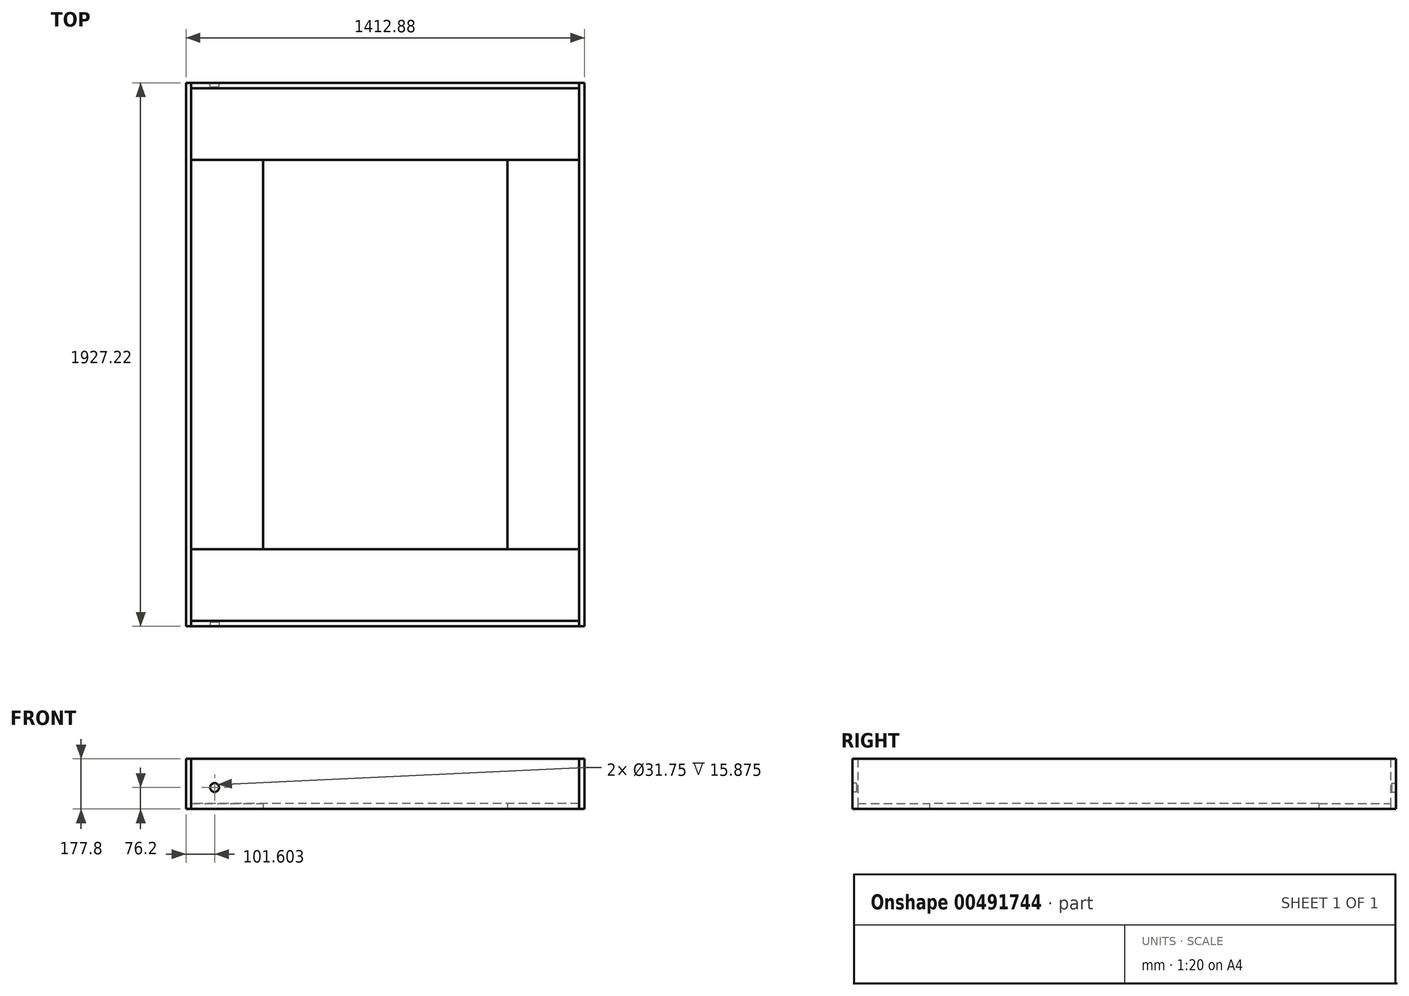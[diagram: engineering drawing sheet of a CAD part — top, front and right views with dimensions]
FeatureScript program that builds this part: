
annotation { "Feature Type Name" : "Feature", "Feature Type Description" : "" }
export const myFeature = defineFeature(function(context is Context, id is Id, definition is map)
    precondition{}
    {
        {
            var Q0;
            Q0=qCreatedBy(makeId("Top.planeOp"),FACE);
            var sketch = newSketch(context, id + "F0", { "sketchPlane" : qUnion([Q0])});
            skLineSegment(sketch, "E0.bottom", {"start": v(687.39, -944.56) * mm, "end": v(-687.39, -944.56) * mm});
            skLineSegment(sketch, "E0.top", {"start": v(687.39, 944.56) * mm, "end": v(-687.39, 944.56) * mm});
            skLineSegment(sketch, "E0.left", {"start": v(687.39, -944.56) * mm, "end": v(687.39, -690.56) * mm});
            skLineSegment(sketch, "E0.right", {"start": v(-687.39, -944.56) * mm, "end": v(-687.39, -690.56) * mm});
            skPoint(sketch, "E0.middle", {"position": v(0, 0) * mm});
            skLineSegment(sketch, "E1", {"start": v(-687.39, -690.56) * mm, "end": v(687.39, -690.56) * mm});
            skLineSegment(sketch, "E2", {"start": v(-687.39, 690.56) * mm, "end": v(687.39, 690.56) * mm});
            skLineSegment(sketch, "E3.trimOffspring", {"start": v(-687.39, 690.56) * mm, "end": v(-687.39, 944.56) * mm});
            skLineSegment(sketch, "E4.trimOffspring", {"start": v(687.39, 690.56) * mm, "end": v(687.39, 944.56) * mm});
            skSolve(sketch);
        }
        {
            var Q0;
            Q0 = qSketchRegion(id + "F0", true);
            extrude(context, id + "F1", {"entities" : qUnion([Q0]), "depth" : 19.05 * mm});
        }
        {
            var Q0;
            Q0=qCreatedBy(makeId("Top.planeOp"),FACE);
            var sketch = newSketch(context, id + "F2", { "sketchPlane" : qUnion([Q0])});
            skLineSegment(sketch, "E5.bottom", {"start": v(-687.39, 690.56) * mm, "end": v(-433.39, 690.56) * mm});
            skLineSegment(sketch, "E5.top", {"start": v(-687.39, -690.56) * mm, "end": v(-433.39, -690.56) * mm});
            skLineSegment(sketch, "E5.left", {"start": v(-687.39, 690.56) * mm, "end": v(-687.39, -690.56) * mm});
            skLineSegment(sketch, "E5.right", {"start": v(-433.39, 690.56) * mm, "end": v(-433.39, -690.56) * mm});
            skLineSegment(sketch, "E6.bottom", {"start": v(687.39, 690.56) * mm, "end": v(433.39, 690.56) * mm});
            skLineSegment(sketch, "E6.top", {"start": v(687.39, -690.56) * mm, "end": v(433.39, -690.56) * mm});
            skLineSegment(sketch, "E6.left", {"start": v(687.39, 690.56) * mm, "end": v(687.39, -690.56) * mm});
            skLineSegment(sketch, "E6.right", {"start": v(433.39, 690.56) * mm, "end": v(433.39, -690.56) * mm});
            skSolve(sketch);
        }
        {
            var Q0;
            Q0 = qSketchRegion(id + "F2", true);
            var Q1;
            Q1=makeQuery(id+"F1.opExtrude","CAP_FACE",FACE,{"disambiguationData":[OSD([sQuery(id+"F0.wireOp",EDGE,"E0.bottom"),sQuery(id+"F0.wireOp",EDGE,"E0.left"),sQuery(id+"F0.wireOp",EDGE,"E0.right"),sQuery(id+"F0.wireOp",EDGE,"E1")])],"isStart":false});
            extrude(context, id + "F3", {"entities" : qUnion([Q0]), "endBound" : BoundingType.UP_TO_SURFACE, "endBoundEntityFace" : qUnion([Q1]), "depth" : 25.4 * mm});
        }
        {
            var Q0;
            Q0=qCreatedBy(makeId("Top.planeOp"),FACE);
            var sketch = newSketch(context, id + "F4", { "sketchPlane" : qUnion([Q0])});
            skLineSegment(sketch, "E7.bottom", {"start": v(-706.44, 963.61) * mm, "end": v(-687.39, 963.61) * mm});
            skLineSegment(sketch, "E7.top", {"start": v(-706.44, -963.61) * mm, "end": v(-687.39, -963.61) * mm});
            skLineSegment(sketch, "E7.left", {"start": v(-706.44, 963.61) * mm, "end": v(-706.44, -963.61) * mm});
            skLineSegment(sketch, "E7.right", {"start": v(-687.39, 963.61) * mm, "end": v(-687.39, -963.61) * mm});
            skLineSegment(sketch, "E8.bottom", {"start": v(687.39, 963.61) * mm, "end": v(706.44, 963.61) * mm});
            skLineSegment(sketch, "E8.top", {"start": v(687.39, -963.61) * mm, "end": v(706.44, -963.61) * mm});
            skLineSegment(sketch, "E8.left", {"start": v(687.39, 963.61) * mm, "end": v(687.39, -963.61) * mm});
            skLineSegment(sketch, "E8.right", {"start": v(706.44, 963.61) * mm, "end": v(706.44, -963.61) * mm});
            skSolve(sketch);
        }
        {
            var Q0;
            Q0 = qSketchRegion(id + "F4", true);
            extrude(context, id + "F5", {"entities" : qUnion([Q0]), "depth" : 177.8 * mm});
        }
        {
            var Q0;
            Q0=qCreatedBy(makeId("Top.planeOp"),FACE);
            var sketch = newSketch(context, id + "F6", { "sketchPlane" : qUnion([Q0])});
            skLineSegment(sketch, "E9.bottom", {"start": v(-687.39, -963.61) * mm, "end": v(687.39, -963.61) * mm});
            skLineSegment(sketch, "E9.top", {"start": v(-687.39, -944.56) * mm, "end": v(687.39, -944.56) * mm});
            skLineSegment(sketch, "E9.left", {"start": v(-687.39, -963.61) * mm, "end": v(-687.39, -944.56) * mm});
            skLineSegment(sketch, "E9.right", {"start": v(687.39, -963.61) * mm, "end": v(687.39, -944.56) * mm});
            skLineSegment(sketch, "E10.bottom", {"start": v(-687.39, 963.61) * mm, "end": v(687.39, 963.61) * mm});
            skLineSegment(sketch, "E10.top", {"start": v(-687.39, 944.56) * mm, "end": v(687.39, 944.56) * mm});
            skLineSegment(sketch, "E10.left", {"start": v(-687.39, 963.61) * mm, "end": v(-687.39, 944.56) * mm});
            skLineSegment(sketch, "E10.right", {"start": v(687.39, 963.61) * mm, "end": v(687.39, 944.56) * mm});
            skSolve(sketch);
        }
        {
            var Q0;
            Q0 = qSketchRegion(id + "F6", true);
            var Q1;
            Q1=makeQuery(id+"F5.opExtrude","CAP_FACE",FACE,{"disambiguationData":[OSD([sQuery(id+"F4.wireOp",EDGE,"E7.bottom"),sQuery(id+"F4.wireOp",EDGE,"E7.top"),sQuery(id+"F4.wireOp",EDGE,"E7.left"),sQuery(id+"F4.wireOp",EDGE,"E7.right")])],"isStart":false});
            extrude(context, id + "F7", {"entities" : qUnion([Q0]), "endBound" : BoundingType.UP_TO_SURFACE, "endBoundEntityFace" : qUnion([Q1]), "depth" : 25.4 * mm});
        }
        {
            var Q0;
            Q0=makeQuery(id+"F7.opExtrude","SWEPT_FACE",FACE,{"disambiguationData":[OSD([sQuery(id+"F6.wireOp",EDGE,"E9.bottom")])]});
            var sketch = newSketch(context, id + "F8", { "sketchPlane" : qUnion([Q0])});
            skCircle(sketch, "E11", {"center": v(-604.84, 76.2) * mm, "radius": 15.88 * mm});
            skSolve(sketch);
        }
        {
            var Q0;
            Q0 = qSketchRegion(id + "F8", true);
            extrude(context, id + "F9", {"entities" : qUnion([Q0]), "operationType" : NewBodyOperationType.REMOVE, "oppositeDirection" : true, "depth" : 15.88 * mm});
        }
        {
            var Q0;
            Q0=makeQuery(id+"F7.opExtrude","SWEPT_FACE",FACE,{"disambiguationData":[OSD([sQuery(id+"F6.wireOp",EDGE,"E10.bottom")])]});
            var sketch = newSketch(context, id + "F10", { "sketchPlane" : qUnion([Q0])});
            skCircle(sketch, "E12.0", {"center": v(604.84, 76.2) * mm, "radius": 15.88 * mm});
            skSolve(sketch);
        }
        {
            var Q0;
            Q0 = qSketchRegion(id + "F10", true);
            extrude(context, id + "F11", {"entities" : qUnion([Q0]), "operationType" : NewBodyOperationType.REMOVE, "oppositeDirection" : true, "depth" : 15.88 * mm});
        }
    });
